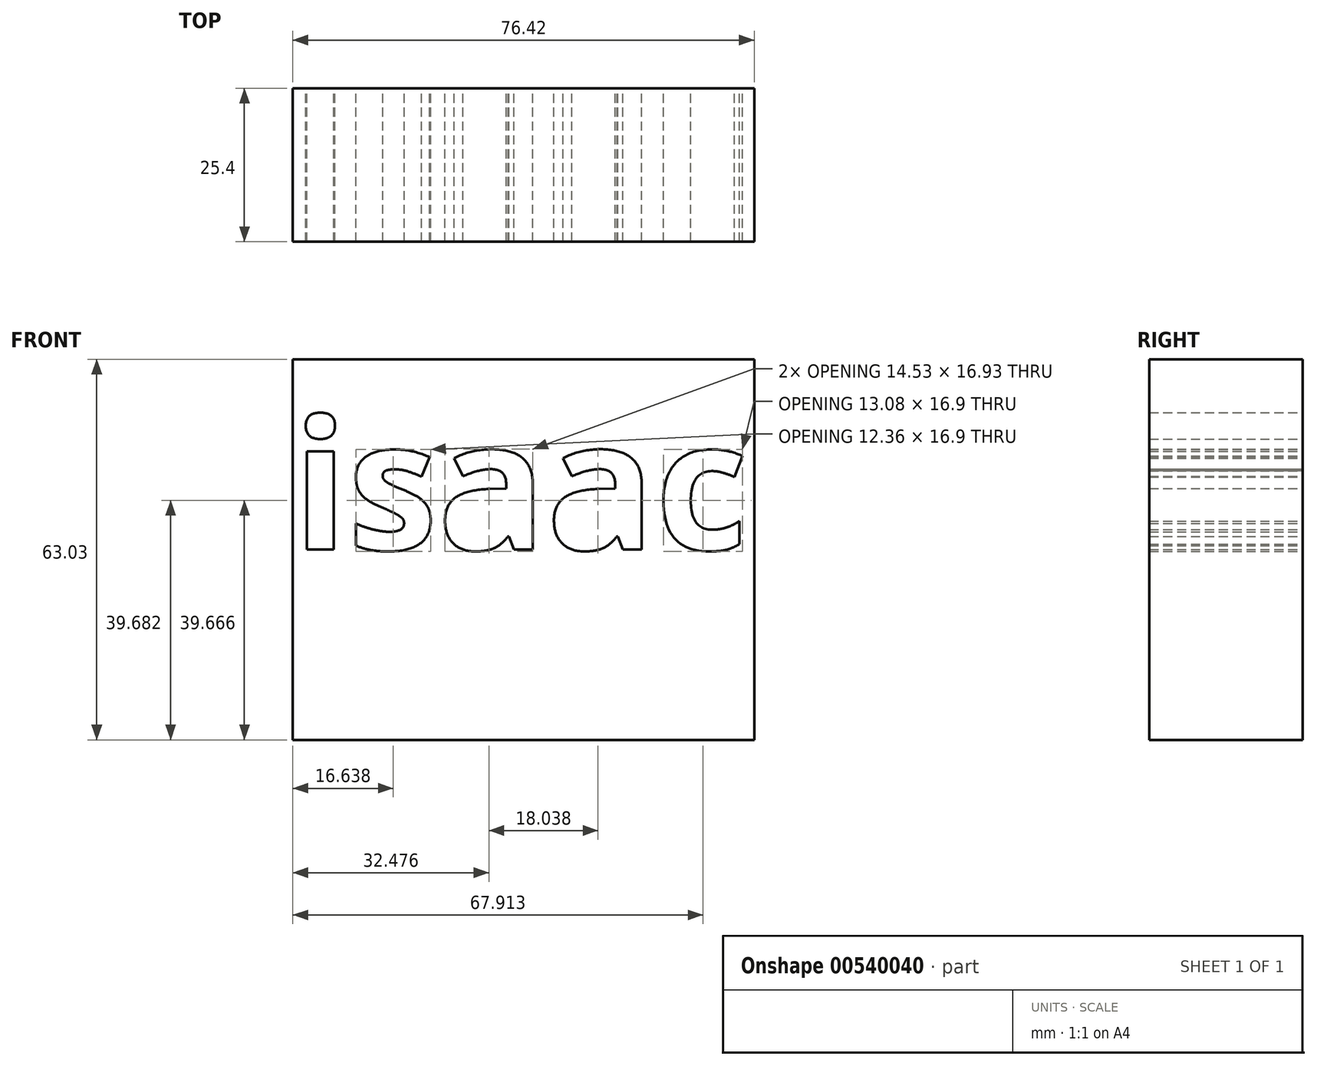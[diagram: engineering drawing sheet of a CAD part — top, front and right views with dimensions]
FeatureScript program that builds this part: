
annotation { "Feature Type Name" : "Feature", "Feature Type Description" : "" }
export const myFeature = defineFeature(function(context is Context, id is Id, definition is map)
    precondition{}
    {
        {
            var Q0;
            Q0=qCreatedBy(makeId("Front.planeOp"),FACE);
            var sketch = newSketch(context, id + "F0", { "sketchPlane" : qUnion([Q0])});
            skLineSegment(sketch, "E0.bottom", {"start": v(0, 0) * mm, "end": v(76.42, 0) * mm});
            skLineSegment(sketch, "E0.top", {"start": v(0, 63.03) * mm, "end": v(76.42, 63.03) * mm});
            skLineSegment(sketch, "E0.left", {"start": v(0, 0) * mm, "end": v(0, 63.03) * mm});
            skLineSegment(sketch, "E0.right", {"start": v(76.42, 0) * mm, "end": v(76.42, 63.03) * mm});
            skText(sketch, "E1", { "text": "isaac", "fontName": "OpenSans-Bold.ttf"});
            const initialGuessF0  = {"E1": [0, 0.03151, 1, 0, 0.0215]};
            skSetInitialGuess(sketch, initialGuessF0);
            skSolve(sketch);
        }
        {
            var Q0;
            Q0 = qSketchRegion(id + "F0", true);
            extrude(context, id + "F1", {"entities" : qUnion([Q0]), "depth" : 25.4 * mm, "offsetDistance" : 25.4 * mm});
        }
    });
